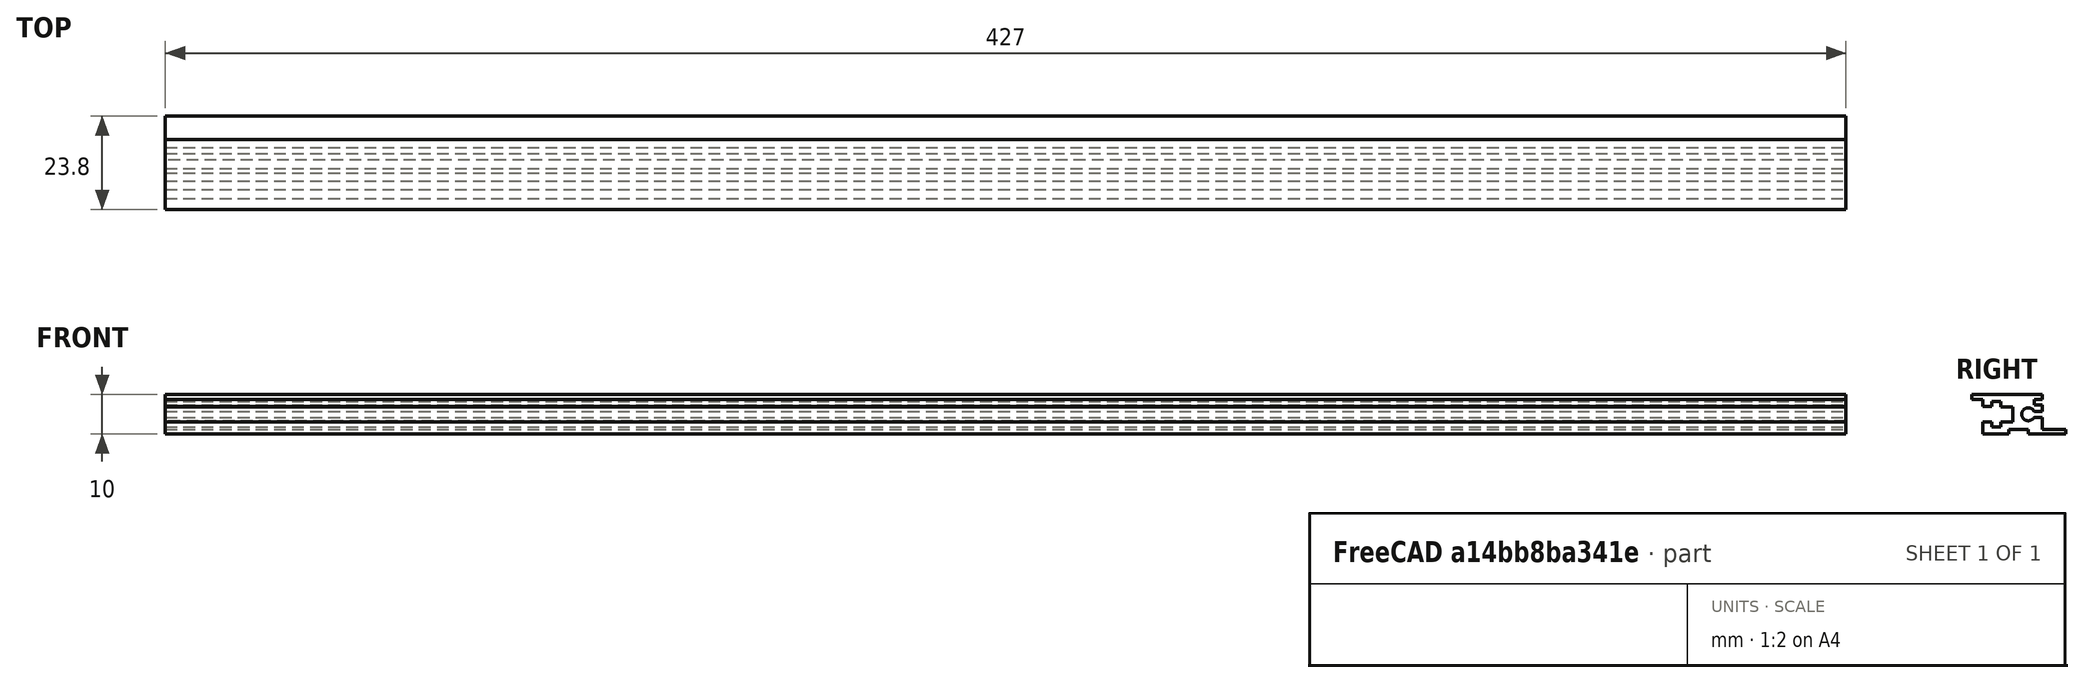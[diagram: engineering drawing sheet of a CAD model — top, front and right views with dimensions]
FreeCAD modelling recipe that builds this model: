
FCSTD DOCUMENT  (FreeCAD 1.0R38641 +468 (Git))
Label: tiptop_z_rail
License: All rights reserved
LicenseURL: https://en.wikipedia.org/wiki/All_rights_reserved
objects: Sketcher::SketchObject×1, PartDesign::Pad×1, PartDesign::Body×1, App::VarSet×1
note: 6 computed .brp shape members not serialized (recipe doc carries the construction recipe); baked Part::Feature solids carry a one-line shape summary decoded from their .brp

FEATURE [Sketcher::SketchObject] Sketch
  ArcFitTolerance = 1e-06
  FullyConstrained = false
  MakeInternals = false
  Placement = pos=(0,0,0) rot=(0.57735,0.57735,0.57735;2.0944rad)
  sketch-geometry (32):
    g0: LineSegment StartX=2.8 StartY=0 StartZ=0 EndX=9.3 EndY=0 EndZ=0
    g1: LineSegment StartX=9.3 StartY=0 StartZ=0 EndX=9.3 EndY=1.2 EndZ=0
    g2: LineSegment StartX=9.3 StartY=1.2 StartZ=0 EndX=14.3 EndY=1.2 EndZ=0
    g3: LineSegment StartX=14.3 StartY=1.2 StartZ=0 EndX=14.3 EndY=0 EndZ=0
    g4: LineSegment StartX=14.3 StartY=0 StartZ=0 EndX=23.8 EndY=0 EndZ=0
    g5: LineSegment StartX=23.8 StartY=0 StartZ=0 EndX=23.8 EndY=1.2 EndZ=0
    g6: LineSegment StartX=23.8 StartY=1.2 StartZ=0 EndX=17.8 EndY=1.2 EndZ=0
    g7: LineSegment StartX=17.8 StartY=1.2 StartZ=0 EndX=17.8 EndY=4.24198 EndZ=0
    g8: LineSegment StartX=17.8 StartY=7.4 StartZ=0 EndX=15.8 EndY=7.4 EndZ=0
    g9: LineSegment StartX=2.8 StartY=0 StartZ=0 EndX=2.8 EndY=3 EndZ=0
    g10: LineSegment StartX=2.8 StartY=3 StartZ=0 EndX=5.07531 EndY=3 EndZ=0
    g11: LineSegment StartX=5.07531 StartY=3 StartZ=0 EndX=5.07531 EndY=1.75 EndZ=0
    g12: LineSegment StartX=5.07531 StartY=1.75 StartZ=0 EndX=7.28837 EndY=1.75 EndZ=0
    g13: LineSegment StartX=7.28837 StartY=1.75 StartZ=0 EndX=7.28837 EndY=3 EndZ=0
    g14: LineSegment StartX=7.28837 StartY=3 StartZ=0 EndX=10.4 EndY=3 EndZ=0
    g15: LineSegment StartX=10.4 StartY=3 StartZ=0 EndX=10.4 EndY=6.84125 EndZ=0
    g16: LineSegment StartX=10.4 StartY=6.84125 StartZ=0 EndX=7.28837 EndY=6.84125 EndZ=0
    g17: LineSegment StartX=7.28837 StartY=6.84125 StartZ=0 EndX=7.28837 EndY=8.25 EndZ=0
    g18: LineSegment StartX=7.28837 StartY=8.25 StartZ=0 EndX=5.07531 EndY=8.25 EndZ=0
    g19: LineSegment StartX=5.07531 StartY=8.25 StartZ=0 EndX=5.07531 EndY=7 EndZ=0
    g20: LineSegment StartX=5.07531 StartY=7 StartZ=0 EndX=2.8 EndY=7 EndZ=0
    g21: LineSegment StartX=2.8 StartY=7 StartZ=0 EndX=2.8 EndY=8.8 EndZ=0
    g22: LineSegment StartX=2.8 StartY=8.8 StartZ=0 EndX=0 EndY=8.8 EndZ=0
    g23: LineSegment StartX=0 StartY=8.8 StartZ=0 EndX=0 EndY=10 EndZ=0
    g24: LineSegment StartX=0 StartY=10 StartZ=0 EndX=17.8 EndY=10 EndZ=0
    g25: LineSegment StartX=17.8 StartY=10 StartZ=0 EndX=17.8 EndY=8.8 EndZ=0
    g26: LineSegment StartX=17.8 StartY=8.8 StartZ=0 EndX=15.8 EndY=8.8 EndZ=0
    g27: LineSegment StartX=15.8 StartY=8.8 StartZ=0 EndX=15.8 EndY=7.4 EndZ=0
    g28: LineSegment StartX=17.8 StartY=7.4 StartZ=0 EndX=17.8 EndY=5.75802 EndZ=0
    g29: LineSegment StartX=17.8 StartY=5.75802 StartZ=0 EndX=15.7656 EndY=5.75802 EndZ=0
    g30: LineSegment StartX=17.8 StartY=4.24198 StartZ=0 EndX=15.7656 EndY=4.24198 EndZ=0
    g31: ArcOfCircle CenterX=14.3 CenterY=5 CenterZ=0 NormalX=0 NormalY=0 NormalZ=1 AngleXU=0 Radius=1.65 StartAngle=0.477326 EndAngle=5.80586
  constraints (92):
    c: PointOnObject(g0,g-1)
    c: PointOnObject(g0,g-1)
    c: Coincident(g0,g1)
    c: Vertical(g1)
    c: Coincident(g1,g2)
    c: Horizontal(g2)
    c: Coincident(g2,g3)
    c: PointOnObject(g3,g-1)
    c: Vertical(g3)
    c: Coincident(g3,g4)
    c: PointOnObject(g4,g-1)
    c: Coincident(g4,g5)
    c: Vertical(g5)
    c: Coincident(g5,g6)
    c: Horizontal(g6)
    c: Coincident(g6,g7)
    c: Vertical(g7)
    c: Horizontal(g8)
    c: Coincident(g0,g9)
    c: Vertical(g9)
    c: Coincident(g9,g10)
    c: Horizontal(g10)
    c: Coincident(g10,g11)
    c: Vertical(g11)
    c: Coincident(g11,g12)
    c: Horizontal(g12)
    c: Coincident(g12,g13)
    c: Vertical(g13)
    c: Coincident(g13,g14)
    c: Horizontal(g14)
    c: Coincident(g14,g15)
    c: Vertical(g15)
    c: Coincident(g15,g16)
    c: Horizontal(g16)
    c: Coincident(g16,g17)
    c: Vertical(g17)
    c: Coincident(g17,g18)
    c: Horizontal(g18)
    c: Coincident(g18,g19)
    c: Vertical(g19)
    c: Coincident(g19,g20)
    c: Horizontal(g20)
    c: Coincident(g20,g21)
    c: Coincident(g21,g22)
    c: PointOnObject(g22,g-2)
    c: Horizontal(g22)
    c: Coincident(g22,g23)
    c: PointOnObject(g23,g-2)
    c: Coincident(g23,g24)
    c: Horizontal(g24)
    c: Coincident(g24,g25)
    c: Coincident(g25,g26)
    c: Horizontal(g26)
    c: Coincident(g26,g27)
    c: Coincident(g27,g8)
    c: Vertical(g27)
    c: DistanceY(g23,g23) = 1.2  'LipHeight'
    c: DistanceX(g22,g22) = 2.8
    c: DistanceY(g9,g20) = 4
    c: DistanceY(g9,g9) = 3
    c: DistanceX(g21,g15) = 7.6
    c: Distance(g12,g18) = 6.5
    c: DistanceX(g2,g2) = 5
    c: DistanceY(g1,g1) = 1.2
    c: DistanceX(g6,g6) = 6
    c: Distance(g25,g25) = 1.2
    c: DistanceY(g27,g27) = 1.4
    c: Coincident(g8,g28)
    c: Coincident(g28,g29)
    c: Horizontal(g29)
    c: Coincident(g7,g30)
    c: Horizontal(g30)
    c: Coincident(g31,g29)
    c: Coincident(g31,g30)
    c: DistanceX(g4,g4) = 9.5
    c: Distance(g5,g-2) = 23.8
    c: Diameter(g31) = 3.3  'RailHoleDIameter'
    c: DistanceX(g26,g26) = 2
    c: DistanceX(g31,g24) = 3.5
    c: DistanceY(g31,g24) = 5
    c: DistanceY(g6,g31) = 3.8
    c: DistanceY(g-1,g23) = 10
    c: Tangent(g7,g28)
    c: Tangent(g25,g28)
    c: Tangent(g9,g21)
    c: Equal(g30,g29)
    c: Equal(g11,g13)
    c: Equal(g11,g19)
    c: Equal(g18,g12)
    c: Equal(g14,g16)
    c: DistanceY(g31,g23) = 5  'RailTopToHoleCenterY'
    c: DistanceX(g23,g31) = 14.3  'LipToHoleCenterX'
FEATURE [PartDesign::Pad] Pad
  Direction = (1,1e-16,-1e-16)
  Length = 427
  Length2 = 10
  Placement = pos=(0,0,0) rot=(0.57735,0.57735,0.57735;2.0944rad)
  Profile = -> Sketch
  ReferenceAxis = -> Sketch [N_Axis]
  Refine = true
  Suppressed = false
  Type = 0
  expr: Length = VarSet.RailLength
FEATURE [PartDesign::Body] Body  label="ZRail84Hp"
  AllowCompound = false
  Group = -> [Sketch,Pad]
  Origin = -> Origin
  Tip = -> Pad
FEATURE [App::VarSet] VarSet
  RailLength = 427
